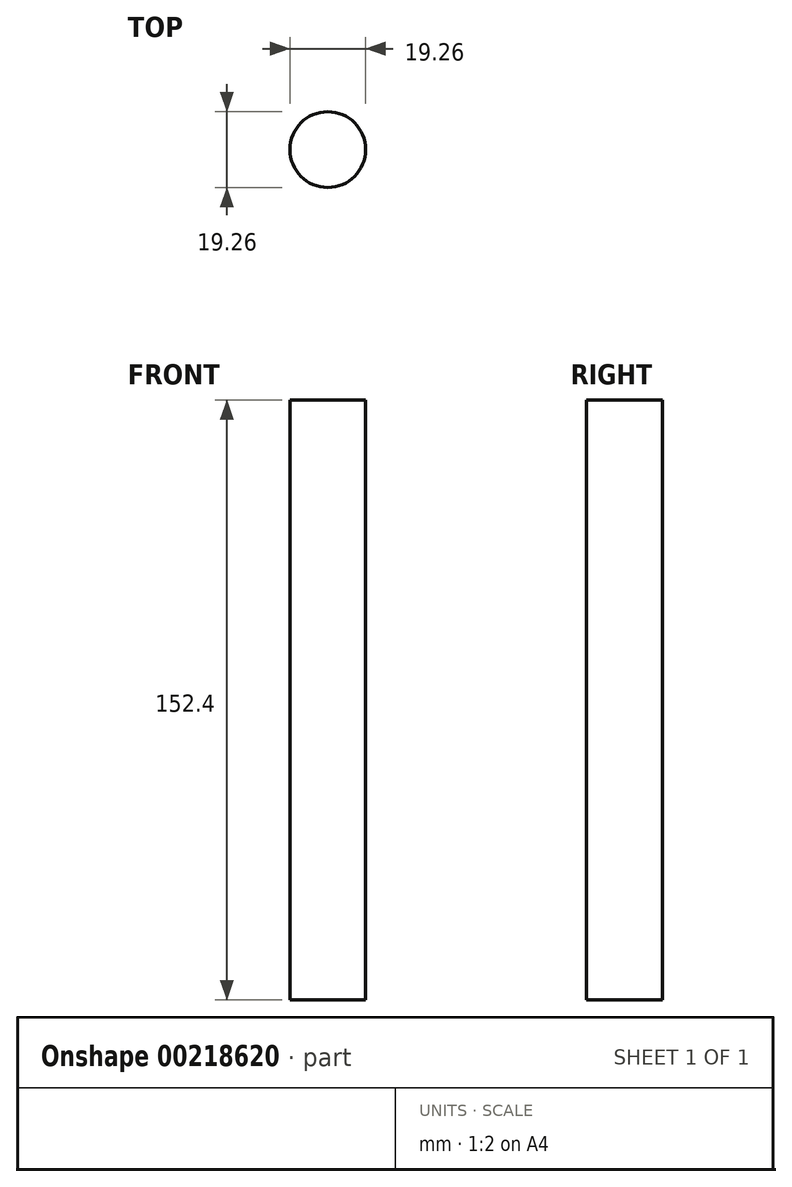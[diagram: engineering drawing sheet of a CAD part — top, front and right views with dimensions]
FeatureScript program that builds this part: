
annotation { "Feature Type Name" : "Feature", "Feature Type Description" : "" }
export const myFeature = defineFeature(function(context is Context, id is Id, definition is map)
    precondition{}
    {
        {
            var Q0;
            Q0=qCreatedBy(makeId("Top.planeOp"),FACE);
            var sketch = newSketch(context, id + "F0", { "sketchPlane" : qUnion([Q0])});
            skCircle(sketch, "E0", {"center": v(0, 0) * mm, "radius": 9.63 * mm});
            skSolve(sketch);
        }
        {
            var Q0;
            Q0=makeQuery(id+"F0.imprint","IMPRINT",FACE,{"disambiguationData":[TD([[makeQuery(id+"F0.imprint","IMPRINT",EDGE,{"derivedFrom":sQuery(id+"F0.wireOp",EDGE,"E0")}),1.0]])]});
            extrude(context, id + "F1", {"entities" : qUnion([Q0]), "depth" : 152.4 * mm, "offsetDistance" : 25 * mm});
        }
    });
